# Revit family: Legrand - Distribution envelopes XL³ S 4000 Cable sheath L350xh2000
name_source: partatom
category: Equipement électrique
units: mm (PartAtom-declared; Revit-internal decimal feet)

## family parameters
Basée sur le plan de construction = Non
Configuration du panneau = Deux colonnes, circuits au sein
Cote de connecteur circulaire = Utiliser le diamètre
Couper avec des vides une fois chargée = Non
Numéro OmniClass = 23.80.30.11.17
Partagée = Non
Point de calcul de pièce = Non
Titre OmniClass = Distribution Boards and Control Panels
Toujours verticalement = Oui
Type d'élément = Tableau de raccordement

## types (3) — shared parameters
ETIM Class 6.0 = EC000261
Fabricant = Legrand
General Conditions of Use = https://export.legrand.com
IK = 07
IP = 40
Material = Steel
RAL = 9003
URL = www.legrand.fr
door = Oui
finish kit = Non
finish kit depth 400mm = Non
finish kit depth 600mm = Non
finish kit depth 800mm = Non
left side panel = Oui
plinth 100mm = Non
plinth 200mm = Non
plinth depth 400mm = Non
plinth depth 400mm height 200mm = Non
plinth depth 600mm = Non
plinth depth 600mm height 200mm = Non
plinth depth 800mm = Non
plinth depth 800mm height 200mm = Non
rear panel = Oui
right side panel = Oui
zero-valued in all types: Elévation par défaut, hauteur socle

## per-type parameters (varying)
| type | Description | depth 400mm | depth 600mm | depth 800mm | door depth 400mm | door depth 600mm | door depth 800mm | left side panel depth 400mm | left side panel depth 600mm | left side panel depth 800mm | right side panel depth 400mm | right side panel depth 600mm | right side panel depth 800mm | structure 338000 | structure 338004 | structure 338008 |
| XL³ S 4000 - Cable sheath - Metal - Height 2000mm - Width 350mm - Depth 400mm | Ref 338001 + 338080 + 338061 + 338100 -XL³ S 4000 - Cable sheath - Metal - Height 2000mm - Width 350mm - Depth 400mm | Oui | Non | Non | Oui | Non | Non | Oui | Non | Non | Oui | Non | Non | Oui | Non | Non |
| XL³ S 4000 - Cable sheath - Metal - Height 2000mm - Width 350mm - Depth 600mm | Ref 338005 + 338080 + 338062 + 338100 - XL³ S 4000 - Cable sheath - Metal - Height 2000mm - Width 350mm - Depth 600mm | Non | Oui | Non | Non | Oui | Non | Non | Oui | Non | Non | Oui | Non | Non | Oui | Non |
| XL³ S 4000 - Cable sheath - Metal - Height 2000mm - Width 350mm - Depth 800mm | Ref 338009 + 338080 + 338063 + 338100 -XL³ S 4000 - Cable sheath - Metal - Height 2000mm - Width 350mm - Depth 800mm | Non | Non | Oui | Non | Non | Oui | Non | Non | Oui | Non | Non | Oui | Non | Non | Oui |
